# Revit family: NBS_GreshamOfficeFurnitureLtd_OffcChrs_Monoko
name_source: partatom
category: Furniture
units: mm (PartAtom-declared; Revit-internal decimal feet)

## family parameters
Always vertical = Yes
Cut with Voids When Loaded = No
Room Calculation Point = No
Shared = No
Work Plane-Based = No

## types (2) — shared parameters
Category = Pr_40_50_12_57:Office chairs
CodePerformance = BS 16139:2013
Color = Brown
Constituents = Seat and back
Description = Reception/ breakout space chair
DurationUnit = year
Features = Lightweight, choice of fabrics
Finish = Lacquered
FrameColour = Natural oak,Walnut
FrameFinish = Clear Lacquer
FrameMaterial = Solid Beech Stained
IfcExportAs = IfcFurnitureType
IfcExportType = CHAIR
Load = 110 kg per seat (maximum)
ManufacturerName = Gresham Office Furniture Ltd
ManufacturerURL = www.gof.co.uk
Material = Wood,Plywood,Foam
NBSCertification = www.nationalbimlibrary.com/cert/3uv2slig
NominalHeight = 800 mm
NominalLength = 815 mm
Recyclability = 100%
SeatsAndBacksMaterial = Seat and Back: CMHR Moulded Foam. Seat Board: Plywood Branded Strap: Real Leather
SustainabilityPerformance = n/a,
Uniclass2015Code = Pr_40_50_12_57
Uniclass2015Title = Office chairs
Uniclass2015Version = Products v1.22
Usage = Guest
Version = 1
WarrantyDescription = Two year
WarrantyDurationUnit = year
zero-valued in all types: Default Elevation

## per-type parameters (varying)
| type | AssetType | BIMObjectName | BaseMaterial | MON1S | MON2S | ModelReference | Name | NominalWidth | SeatMaterial | Width |
| MON1S | Movable | NBS_GreshamOfficeFurnitureLtd_OfficeChairs_Monoko_MON1S | NBS_GreshamOfficeFurnitureLtd_NaturalWood | Yes | No | Monoko_MON1S | OfficeChairs_Monoko_MON1S_GreshamOfficeFurnitureLtd | 680 mm  [stored 2.23097 ft] | NBS_GreshamOfficeFurnitureLtd_Fabric_Red | 680 mm  [stored 2.23097 ft] |
| MON2S | Fixed | NBS_GreshamOfficeFurnitureLtd_OfficeChairs_Monoko_MON2S | NBS_GreshamOfficeFurnitureLtd_WalnutWood | No | Yes | Monoko_MON2S | OfficeChairs_Monoko_MON2S_GreshamOfficeFurnitureLtd | 1360 mm | NBS_GreshamOfficeFurnitureLtd_Fabric_Grey | 1360 mm |

note: [stored X ft] marks values corroborated as IEEE doubles in the binary element streams (Revit-internal decimal feet)

## geometry (parser evidence)
native form markers: Sweep x2
no freeform markers — native parametric forms only
